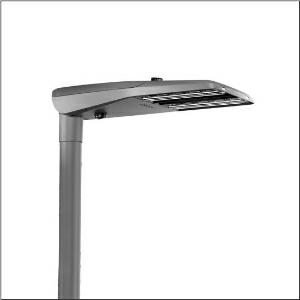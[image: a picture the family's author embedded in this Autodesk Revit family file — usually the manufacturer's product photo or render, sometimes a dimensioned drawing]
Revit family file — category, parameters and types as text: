
# Revit family: streetlight_sl_11_iq_midi___pc-r_5xc3f21y08me_3682
name_source: partatom
category: Lighting Fixtures
units: mm (PartAtom-declared; Revit-internal decimal feet)

## family parameters
Cut with Voids When Loaded = No
Host = Face
Light Source = No
Part Type = Normal
Room Calculation Point = No
Round Connector Dimension = Use Diameter
Shared = No

## types (1)
- --- (1 x LED, 12730 lm, 122.8 W, 2200K)
    Apparent Load = 123 VA
    CIE Flux Codes = 37 73 96 100 100
    Color Rendering = 70
    Color Temperature = 2200K
    Default Elevation = 1800 mm
    Description = Streetlight SL 11 iQ midi, mast luminaire, primary light control with 3 zone facetted reflector, of plastic, silver coated, highly specular, primary optical cover: cover, of PMMA, transparent, light distribution: PC-R, light emission: direct distribution, primary light characteristic: asymmetric, right, installation type: post-top, side-entry, lamps: LED, High Power LED, rated values: 12.730lm | 122,8W | 103,7lm/W (begin service life); end service life: 12.730lm | 130,2W; at 50% lumin. flux: 6.365lm | 56W | 113,7lm/W, colour temperature: 2200K, colour rendering: CRI > 70, light colour: 722, light setting 1 begin service life: 100% | 12.730lm | 122,8W | 103,7lm/W | 2.200K, light setting 1 end service life: 130,2W, further light settings possible, control: pre-setting: logarithmic dimming characteristic, Street-Remote, Auto-Match, Temp-Guard, Lumen-Switch, Night-Set, Smart-Wire, Light-Fading, Desk-Remote (wireless, voltage-free reading and setting of iQ features in the workshop via application-optimized NFC function/RFID function), optimised constant luminous flux control (CLO 2.0), with cable H07RN-F 3x 1.5mm², mains connection: 230..240V, AC, 50/60Hz, connection cable pre-assembled, cable length: 12,5m, luminaire housing, of diecast aluminium, powder-coated, SITECO metallic grey (DB 702S), please order mast flange separately, inclination adjustable without tools: 0°, 5°, 10°, 15° (post-top) | 0°, -5°, -10°, -15° (side-entry), sealing non-destructively replaceable, multi-level sealing system, length: 780mm, width: 376mm, height: 118mm, mast flange for spigot size: 42mm (side-entry): 5XC10008XM4, 60/48mm (side-entry/post-top): 5XC10108XM2, 76/60mm (side-entry/post-top): 5XC10108XM1, equipment: Power, Smart Interface below and above, protection rating (complete): IP66, insulation class (complete): insulation class II (safety insulation), certification: CE, ENEC, ENEC+, VDE, UKCA, impact resistance: IK10, permissible operating ambient temperature for outdoor applications: -25..+50°C, standard-compliant lighting for roads and squares, Environmental Product Declaration (EPD) tested and certified by an independent institute, packaging unit: 1 piece

Light Distribution: PC-R
    Height = 118 mm
    Lamp = 1 x LED
    Lamp Light Flux = 12730 lm
    Lamp Power = 122.8 W
    Lamp count = 1
    Length = 780 mm
    Luminous efficacy = 104 lm/W
    Manufacturer = Siteco
    ModVariant = No
    Model = 5XC3F21Y08ME
    Number of Poles = 1
    OnlyDefault = Yes
    Power Factor = 1
    Product Name = Streetlight SL 11 iQ midi | PC-R
    Product group = mast luminaire | pylon top
    ProductGroupID = 6100
    Protection Class = Protection class II
    Protection Degree = IP 66
    RLX_Detail_Level = 1
    RLX_Emergency_Light_Flux = 0 lm
    RLX_Emergency_Type = 0
    RLX_Emergency_Type_DB = No
    RlxData = <blob elided: 73709 chars, md5=2139624b>
    Socket = socket
    Standby Power = 0 W
    System Light Flux = 12729 lm
    System Power = 123 W
    Type Comments = factory setting: luminous flux: 100 % | dim-lin: 254 | 553 mA
    Type Image = l_1004429.jpg
    URL = http://relux.com
    VarID = @adj_126741
    Voltage = 0 V
    Weight = 0.00 kg
    Width = 376 mm

## geometry (parser evidence)
native form markers: Blend x4, Sweep x9
no freeform markers — native parametric forms only
